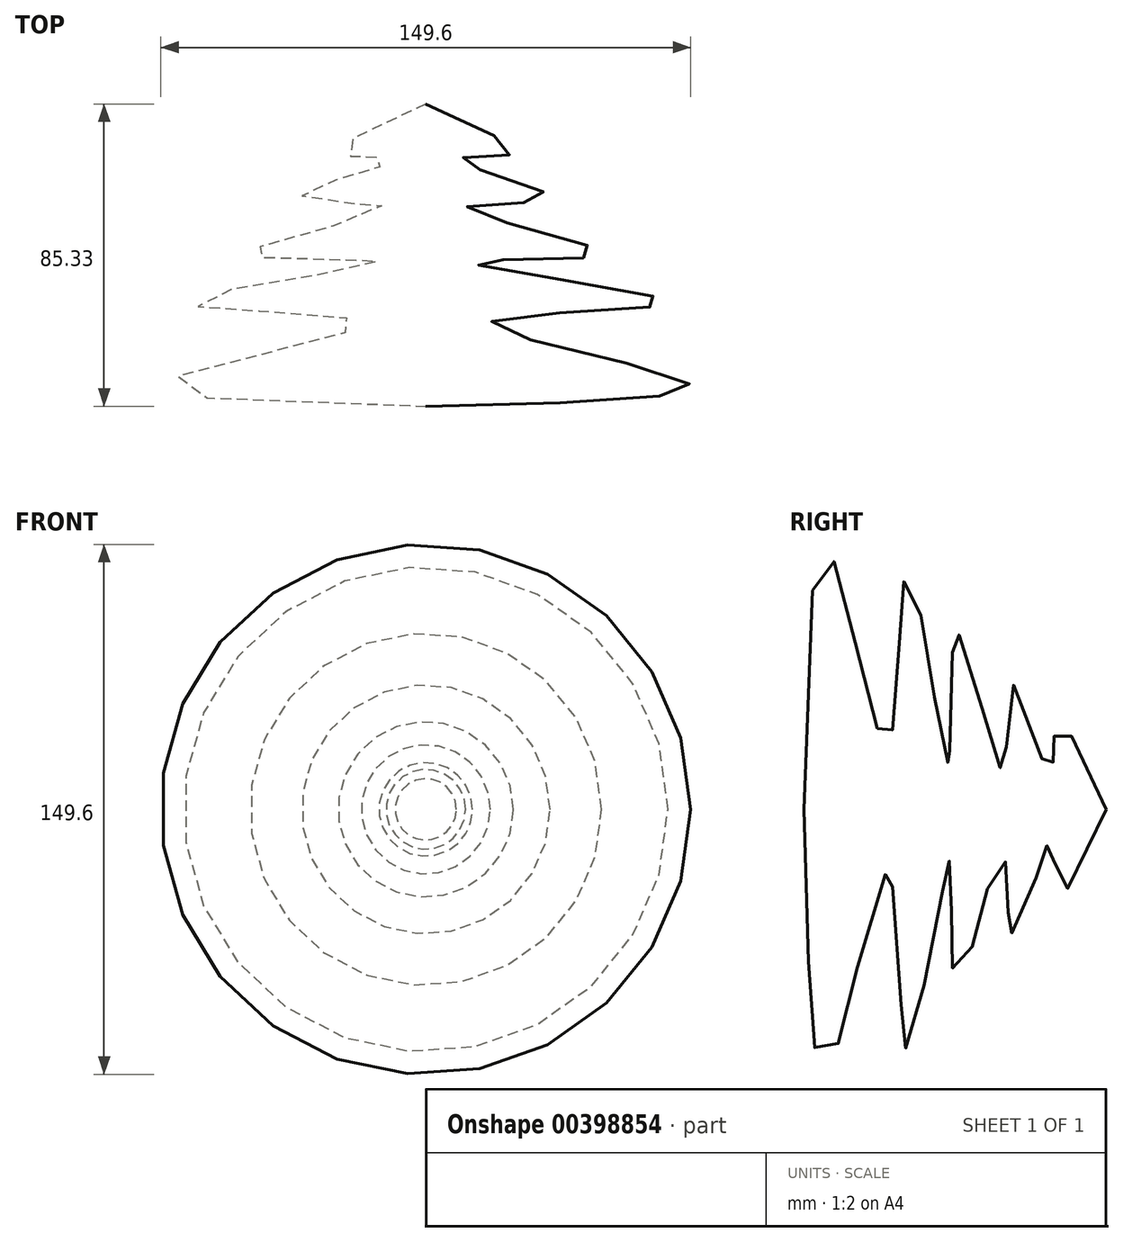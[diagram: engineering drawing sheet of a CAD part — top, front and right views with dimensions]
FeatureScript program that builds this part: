
annotation { "Feature Type Name" : "Feature", "Feature Type Description" : "" }
export const myFeature = defineFeature(function(context is Context, id is Id, definition is map)
    precondition{}
    {
        {
            var Q0;
            Q0=qCreatedBy(makeId("Top.planeOp"),FACE);
            var sketch = newSketch(context, id + "F0", { "sketchPlane" : qUnion([Q0])});
            skLineSegment(sketch, "E0", {"start": v(0, 55.97) * mm, "end": v(0, -29.36) * mm});
            skFitSpline(sketch, "E1", {"points": [v(0, 55.97) * mm, v(24.04, 41.78) * mm, v(8.67, 40.2) * mm, v(35.08, 29.56) * mm, v(11.23, 26.6) * mm, v(49.66, 13.8) * mm, v(13.2, 11.23) * mm, v(68.38, 0) * mm, v(18.33, -5.72) * mm, v(73.3, -22.27) * mm, v(0, -29.36) * mm], "startDerivative": vector(499.42, -220.46) * mm, "endDerivative": vector(-911.21, -19.35) * mm});
            skSolve(sketch);
        }
        {
            var Q0;
            Q0 = qSketchRegion(id + "F0", true);
            var Q1;
            Q1=sQuery(id+"F0.wireOp",EDGE,"E0");
            revolve(context, id + "F1", {"entities" : qUnion([Q0]), "axis" : qUnion([Q1]), "revolveType" : RevolveType.FULL});
        }
    });
